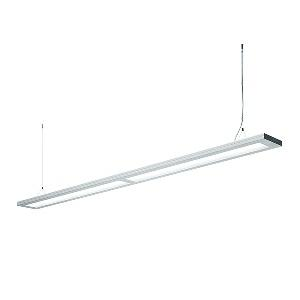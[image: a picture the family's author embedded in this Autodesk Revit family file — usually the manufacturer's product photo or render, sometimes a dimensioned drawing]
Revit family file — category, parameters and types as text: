
# Revit family: lavigo_-_dpp_13000_840_r_g2_00800706_38f7
name_source: partatom
category: Lighting Fixtures
units: mm (PartAtom-declared; Revit-internal decimal feet)

## family parameters
Cut with Voids When Loaded = No
Host = Face
Light Source = No
Part Type = Normal
Room Calculation Point = No
Round Connector Dimension = Use Diameter
Shared = No

## types (1)
- LAVIGO - DPP 13000/840/R/G2 (1 x LED, 13800 lm, 4000K)
    Apparent Load = 97 VA
    Approval mark = CE
    CIE Flux Codes = 60 87 97 25 100
    Color Rendering = 80-89
    Color Temperature = 4000K
    Control Gear = Electronic ballast
    Default Elevation = 1800 mm
    Description = DPP 13000/840/R/G2|Suspended luminaire|light source: LED|connected load: 220-240 V, 50/60 Hz|Power consumption: approx. 97 W|standby: approx. 0,50|luminous flux: 13800 lm|luminous efficacy: 142 lm/W|light distribution: Direct/indirect|direct ratio: approx. 25 %|colour temperature: Cold white, ca. 4000 K|color rendering index (CRI): >= 80|chromaticity tolerance:  3 SDCM|System of protection: IP 20|technology: Presence and daylight sensor control (PIR)|luminaire body|material: Steel/plastic|surface: Powder coatet|colour: White|lamp cover: Polycarbonate (PC), Clear|mains lead: 1.00 m With free stranded wires|Fastening: Steel cable 0.3 - 0.7 m|decorative contrast side parts: Flint grey|glare control: Prism aperture|luminance(L65): <= 2700 cd/m|unified glare rating(4H 8H): <=  16|special features: Canopy colour (pure white), Push button in luminaire head, Cradle to Cradle Certified TM, Direct light component with edge light and light-guide technology for homogenous light exit, Integrated light and presence sensor PIR, Retrofittable with TALK module, Separated, direct and indirect light individually adjustable|
    Frequency = 50 Hz
    Height = 36 mm
    Lamp = 1 x LED
    Lamp Light Flux = 13800 lm
    Lamp count = 1
    Length = 2430 mm
    Luminous efficacy = 142 lm/W
    Manufacturer = Waldmann
    ModVariant = No
    Model = 00800706
    Mounting Place = Ceiling
    Mounting Type = Pendant
    Number of Poles = 1
    OnlyDefault = Yes
    Power Factor = 1
    Product Name = LAVIGO - DPP 13000/840/R/G2
    Product group = Suspended luminaire
    ProductGroupID = 9
    Protection Class = Protection class I
    Protection Degree = IP 20
    RLX_Detail_Level = 1
    RLX_Emergency_Light_Flux = 0 lm
    RLX_Emergency_Type = 0
    RLX_Emergency_Type_DB = No
    RlxData = <blob elided: 25649 chars, md5=3030fbd0>
    Socket = socket
    Standby Power = 0 W
    System Light Flux = 13800 lm
    System Power = 97 W
    Type Comments = Product without accessories
    Type Image = 121742000-00681438.jpg
    URL = http://relux.com
    VarID = ---
    Voltage = 230 V
    Voltage Range = 220-240 V
    Weight = 0.00 kg
    Width = 200 mm  [stored 0.656168 ft]

note: [stored X ft] marks values corroborated as IEEE doubles in the binary element streams (Revit-internal decimal feet)

## geometry (parser evidence)
native form markers: Blend x4, Sweep x12
no freeform markers — native parametric forms only
